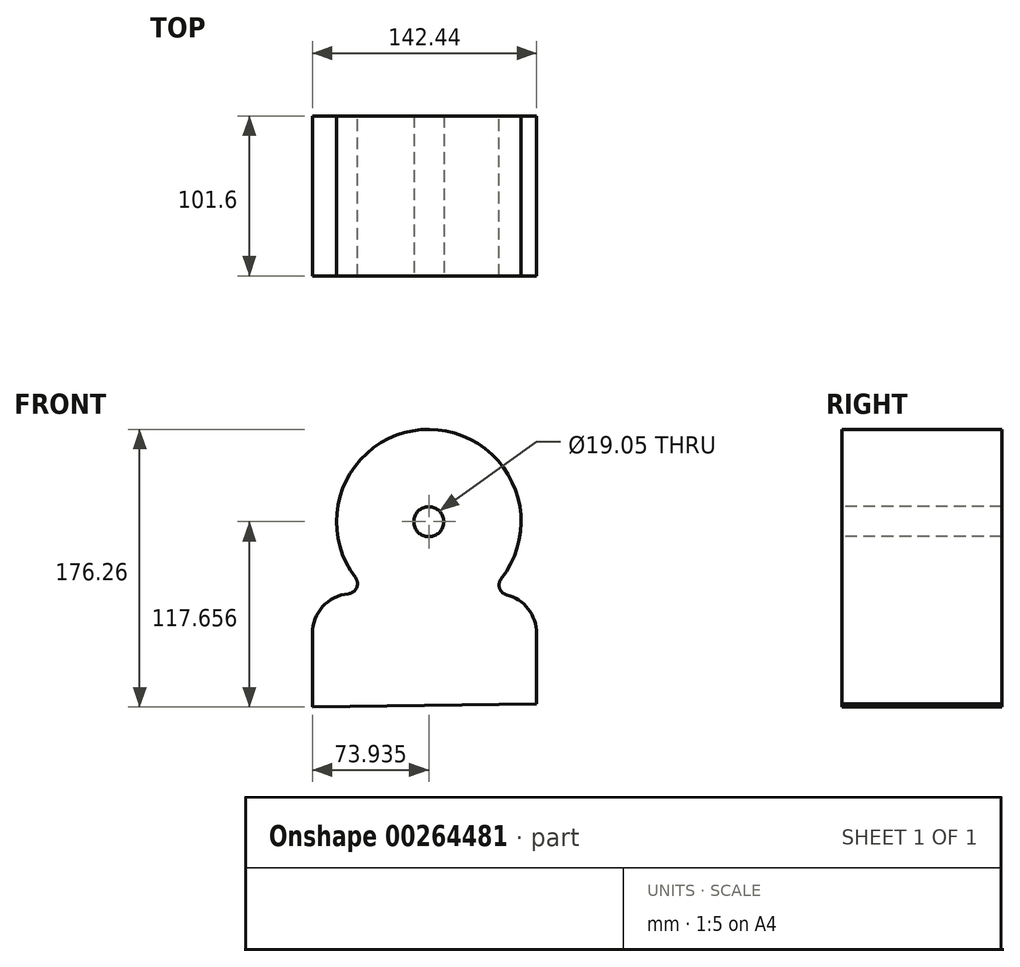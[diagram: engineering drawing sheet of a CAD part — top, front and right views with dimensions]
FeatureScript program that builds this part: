
annotation { "Feature Type Name" : "Feature", "Feature Type Description" : "" }
export const myFeature = defineFeature(function(context is Context, id is Id, definition is map)
    precondition{}
    {
        {
            var Q0;
            Q0=qCreatedBy(makeId("Front.planeOp"),FACE);
            var sketch = newSketch(context, id + "F0", { "sketchPlane" : qUnion([Q0])});
            skLineSegment(sketch, "E0", {"start": v(-130.23, -24.03) * mm, "end": v(-130.23, 48.01) * mm});
            skLineSegment(sketch, "E1", {"start": v(12.2, 48.01) * mm, "end": v(12.2, -22.26) * mm});
            skLineSegment(sketch, "E2", {"start": v(12.2, -22.26) * mm, "end": v(-130.23, -24.03) * mm});
            skArc(sketch, "E3", {"start": v(-19.5, 48.01) * mm, "mid": v(-56.3, 152.23) * mm, "end": v(-93.09, 48.01) * mm});
            skLineSegment(sketch, "E4.trimOffspring", {"start": v(-19.5, 48.01) * mm, "end": v(12.2, 48.01) * mm});
            skLineSegment(sketch, "E5", {"start": v(-130.23, 48.01) * mm, "end": v(-93.09, 48.01) * mm});
            skSolve(sketch);
        }
        {
            var Q0;
            Q0 = qSketchRegion(id + "F0", true);
            extrude(context, id + "F1", {"entities" : qUnion([Q0]), "oppositeDirection" : true, "depth" : 101.6 * mm});
        }
        {
            var Q0;
            Q0=makeQuery(id+"F1.opExtrude","CAP_FACE",FACE,{"disambiguationData":[OSD([sQuery(id+"F0.wireOp",EDGE,"E0"),sQuery(id+"F0.wireOp",EDGE,"E1"),sQuery(id+"F0.wireOp",EDGE,"E2"),sQuery(id+"F0.wireOp",EDGE,"E3"),sQuery(id+"F0.wireOp",EDGE,"E4.trimOffspring"),sQuery(id+"F0.wireOp",EDGE,"E5")])],"isStart":true});
            var sketch = newSketch(context, id + "F2", { "sketchPlane" : qUnion([Q0])});
            skCircle(sketch, "E6", {"center": v(-56.3, 93.63) * mm, "radius": 23.97 * mm});
            skSolve(sketch);
        }
        {
            var Q0;
            Q0=sQuery(id+"F2.wireOp",VERTEX,"E6.center");
            var Q1;
            Q1=makeQuery(id+"F1.opExtrude","SWEPT_BODY",BODY,{"disambiguationData":[OSD([sQuery(id+"F0.wireOp",EDGE,"E0"),sQuery(id+"F0.wireOp",EDGE,"E1"),sQuery(id+"F0.wireOp",EDGE,"E2"),sQuery(id+"F0.wireOp",EDGE,"E3"),sQuery(id+"F0.wireOp",EDGE,"E4.trimOffspring"),sQuery(id+"F0.wireOp",EDGE,"E5")])]});
            hole(context, id + "F3", {"style" : HoleStyle.SIMPLE, "endStyle" : HoleEndStyle.THROUGH, "holeDiameter" : 19.05 * mm, "tappedDepth" : 12.7 * mm, "tapClearance" : 3, "locations" : qUnion([Q0]), "scope" : qUnion([Q1])});
        }
        {
            var Q0;
            Q0=makeQuery(id+"F1.opExtrude","SWEPT_EDGE",EDGE,{"disambiguationData":[OSD([sQuery(id+"F0.wireOp",EDGE,"E0"),sQuery(id+"F0.wireOp",EDGE,"E5")])]});
            var Q1;
            Q1=makeQuery(id+"F1.opExtrude","SWEPT_EDGE",EDGE,{"disambiguationData":[OSD([sQuery(id+"F0.wireOp",EDGE,"E1"),sQuery(id+"F0.wireOp",EDGE,"E4.trimOffspring")])]});
            fillet(context, id + "F4", {"entities" : qUnion([Q0, Q1]), "radius" : 25.4 * mm, "tangentPropagation" : true, "allowEdgeOverflow" : false});
        }
        {
            var Q0;
            Q0=makeQuery(id+"F1.opExtrude","SWEPT_EDGE",EDGE,{"disambiguationData":[OSD([sQuery(id+"F0.wireOp",EDGE,"E3"),sQuery(id+"F0.wireOp",EDGE,"E4.trimOffspring")])]});
            var Q1;
            Q1=makeQuery(id+"F1.opExtrude","SWEPT_EDGE",EDGE,{"disambiguationData":[OSD([sQuery(id+"F0.wireOp",EDGE,"E3"),sQuery(id+"F0.wireOp",EDGE,"E5")])]});
            fillet(context, id + "F5", {"entities" : qUnion([Q0, Q1]), "radius" : 6.35 * mm, "tangentPropagation" : true, "allowEdgeOverflow" : false});
        }
    });
